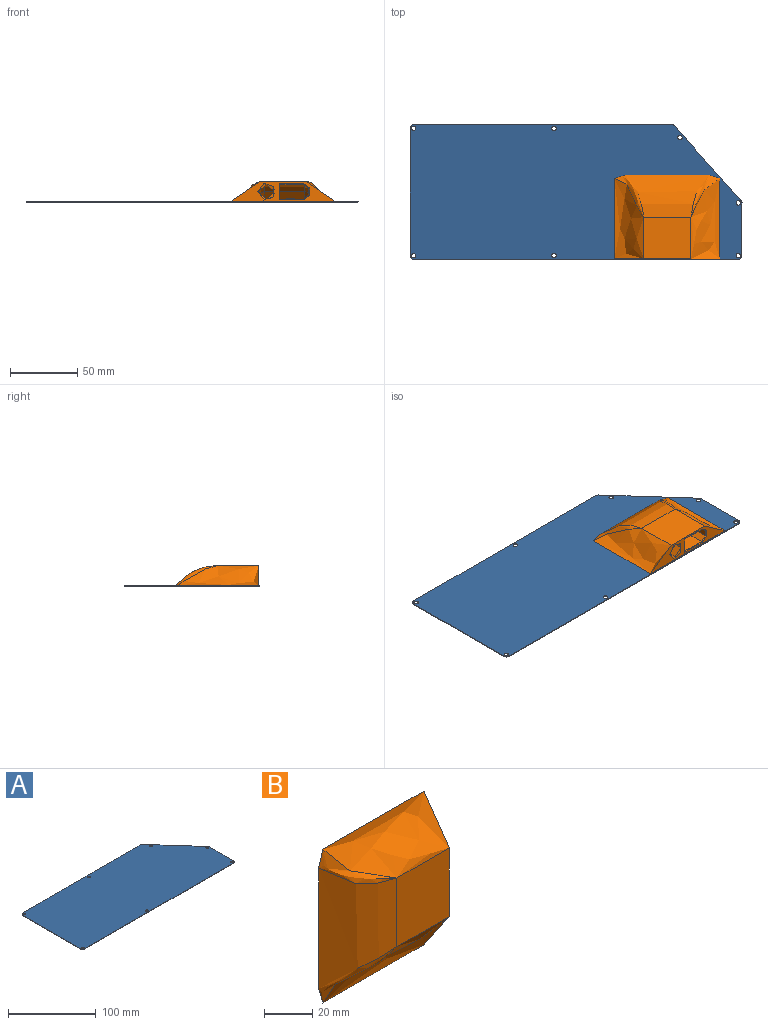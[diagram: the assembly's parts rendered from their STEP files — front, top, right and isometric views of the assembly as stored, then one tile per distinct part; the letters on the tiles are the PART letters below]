
ASSEMBLY  parts=2 mates=1
PART A: 19 faces, bbox 246x100x0.5 mm
  f0: plane 94x0.5mm, normal (-1,0,0), area 47mm2, adj f5,f6,f14,f18
  f1: plane 240x0.5mm, normal (0,-1,0), area 120mm2, adj f5,f6,f14,f15
  f2: plane 38.85x0.5mm, normal (1,0,0), area 19.4mm2, adj f5,f6,f15,f16
  f3: plane 55.15x49.34mm, normal (0.75,0.67,0), area 37mm2, adj f5,f6,f16,f17
  f4: plane 190.66x0.5mm, normal (0,1,0), area 95.3mm2, adj f5,f6,f17,f18
  f5: plane 246x100mm, normal (0,0,1), area 23080.4mm2, adj f0,f1,f2,f3,f4,f7,f8,f9
  f6: plane 246x100mm, normal (0,0,-1), area 23080.4mm2, adj f0,f1,f2,f3,f4,f7,f8,f9
  f7: cylinder r=1.65mm len=3.3mm, axis (0,0,1), area 5.2mm2, adj f5,f6
  f8: cylinder r=1.65mm len=3.3mm, axis (0,0,1), area 5.2mm2, adj f5,f6
  f9: cylinder r=1.65mm len=3.3mm, axis (0,0,1), area 5.2mm2, adj f5,f6
  f10: cylinder r=1.65mm len=3.3mm, axis (0,0,1), area 5.2mm2, adj f5,f6
  f11: cylinder r=1.65mm len=3.3mm, axis (0,0,1), area 5.2mm2, adj f5,f6
  f12: cylinder r=1.65mm len=3.3mm, axis (0,0,1), area 5.2mm2, adj f5,f6
  f13: cylinder r=1.65mm len=3.3mm, axis (0,0,1), area 5.2mm2, adj f5,f6
  f14: cylinder r=3mm len=3mm, axis (0,0,-1), area 2.4mm2, adj f0,f1,f5,f6
  f15: cylinder r=3mm len=3mm, axis (0,0,-1), area 2.4mm2, adj f1,f2,f5,f6
  f16: cylinder r=3mm len=2mm, axis (0,0,-1), area 1.1mm2, adj f2,f3,f5,f6
  f17: cylinder r=3mm len=2.24mm, axis (0,0,-1), area 1.3mm2, adj f3,f4,f5,f6
  f18: cylinder r=3mm len=3mm, axis (0,0,-1), area 2.4mm2, adj f0,f4,f5,f6
PART B: 45 faces, bbox 65.9x20.5x80.6 mm
  f0: plane 24.95x17.2mm, normal (0,-1,0), area 399.1mm2, adj f13,f14,f15,f25,f27,f28,f29,f33
  f1: plane 80.41x64.1mm, normal (0,1,0), area 3804.2mm2, adj f2,f3,f5,f6,f7,f8,f15,f16
  f2: plane 78.31x14.9mm, normal (1,0,0), area 412mm2, adj f1,f3,f4,f5,f32,f33,f34,f35
  f3: extruded ~59.51x21.5mm, area 1248.8mm2, adj f1,f2,f4,f7
  f4: plane 35x30.86mm, normal (0,-1,0), area 1080.1mm2, adj f2,f3,f5,f6,f7
  f5: extruded ~59.51x21.81mm, area 1267.1mm2, adj f1,f2,f4,f8
  f6: bspline ~61.8x31.15mm, area 1720.4mm2, adj f1,f4,f7,f8
  f7: bspline ~32.92x21.5mm, area 187.5mm2, adj f1,f3,f4,f6
  f8: bspline ~32.74x21.96mm, area 85.6mm2, adj f1,f5,f6
  f9: cylinder r=5.85mm len=24.95mm, axis (1,0,0), area 916.9mm2, adj f15,f38
  f10: plane 24.95x5mm, normal (0,0,-1), area 124.7mm2, adj f11,f14,f15,f34
  f11: plane 24.95x4.21mm, normal (0,0.82,-0.57), area 128.3mm2, adj f10,f12,f15,f36
  f12: plane 24.95x17.2mm, normal (0,1,0), area 399.1mm2, adj f11,f13,f15,f21,f22,f24,f31,f37
  f13: plane 24.95x10.9mm, normal (0,0,1), area 271.9mm2, adj f0,f12,f15,f35
  f14: plane 24.95x4.21mm, normal (0,-0.82,-0.57), area 128.3mm2, adj f0,f10,f15,f32
  f15: plane 39.9x13.25mm, normal (-1,0,0), area 189.5mm2, adj f0,f1,f9,f10,f11,f12,f13,f14
  f16: plane 19.28x8.25mm, normal (0,0,-1), area 120.2mm2, adj f1,f15,f42,f43,f44
  f17: plane 19.28x8.25mm, normal (0,0,1), area 120.2mm2, adj f1,f15,f39,f40,f41
  f18: plane 29.9x4.81mm, normal (0,1,0), area 143.9mm2, adj f15,f20,f39,f44
  f19: plane 29.9x7.39mm, normal (0.71,0.71,0), area 312.6mm2, adj f1,f20,f41,f42
  f20: cylinder r=20mm len=29.9mm, axis (0,0,1), area 469.7mm2, adj f18,f19,f40,f43
  f21: plane 5x0.5mm, normal (0,0,1), area 2.4mm2, adj f12,f23,f24,f31
  f22: plane 5x0.5mm, normal (0,0,-1), area 2.4mm2, adj f12,f23,f24,f31
  f23: plane 6x4.5mm, normal (0,1,0), area 27mm2, adj f21,f22,f24,f31
  f24: plane 6x0.5mm, normal (-1,0,0), area 3mm2, adj f12,f21,f22,f23
  f25: plane 5x0.5mm, normal (0,0,1), area 2.4mm2, adj f0,f26,f28,f30
  f26: plane 6x4.5mm, normal (0,-1,0), area 27mm2, adj f25,f27,f28,f30
  f27: plane 5x0.5mm, normal (0,0,-1), area 2.4mm2, adj f0,f26,f28,f29,f30
  f28: plane 6x0.5mm, normal (-1,0,0), area 3mm2, adj f0,f25,f26,f27
  f29: plane 6x0mm, normal (1,0,0), area 0mm2, adj f0,f27,f30
  f30: plane 6x0.5mm, normal (0.71,-0.71,0), area 4.2mm2, adj f25,f26,f27,f29
  f31: plane 6x0.5mm, normal (0.71,0.71,0), area 4.2mm2, adj f12,f21,f22,f23
  f32: plane 4.81x3.55mm, normal (0.71,-0.58,-0.41), area 4.6mm2, adj f2,f14,f33,f34
  f33: plane 17.99x0.6mm, normal (0.71,-0.71,0), area 14.9mm2, adj f0,f2,f32,f35
  f34: plane 5.62x0.6mm, normal (0.71,0,-0.71), area 4.5mm2, adj f2,f10,f32,f36
  f35: plane 12.1x0.6mm, normal (0.71,0,0.71), area 9.8mm2, adj f2,f13,f33,f37
  f36: plane 4.81x3.55mm, normal (0.71,0.58,-0.41), area 4.6mm2, adj f2,f11,f34,f37
  f37: plane 17.99x0.6mm, normal (0.71,0.71,0), area 14.9mm2, adj f2,f12,f35,f36
  f38: cone r=5.85mm half-angle=45deg, axis (1,0,0), area 32.8mm2, adj f2,f9
  f39: cylinder r=5mm len=5mm, axis (-1,0,0), area 37.8mm2, adj f15,f17,f18,f40
  f40: torus R=15mm, axis (0,0,-1), area 112.2mm2, adj f17,f20,f39,f41
  f41: cylinder r=5mm len=10.93mm, axis (-0.71,0.71,0), area 62.5mm2, adj f1,f17,f19,f40
  f42: cylinder r=5mm len=10.93mm, axis (-0.71,0.71,0), area 62.5mm2, adj f1,f16,f19,f43
  f43: torus R=15mm, axis (0,0,-1), area 112.2mm2, adj f16,f20,f42,f44
  f44: cylinder r=5mm len=5mm, axis (1,0,0), area 37.8mm2, adj f15,f16,f18,f43
PLACE A rot(axis=(0.93,0.36,0),0deg) t=(77.08,-64.93,60.09)mm
PLACE B rot(axis=(-0.58,0.58,-0.58),120deg) t=(31.26,-13.57,46.36)mm
MATE planar B.f1 <-> A.f5  axis (0,0,-1) through (31.47,-46.75,60.59)mm
